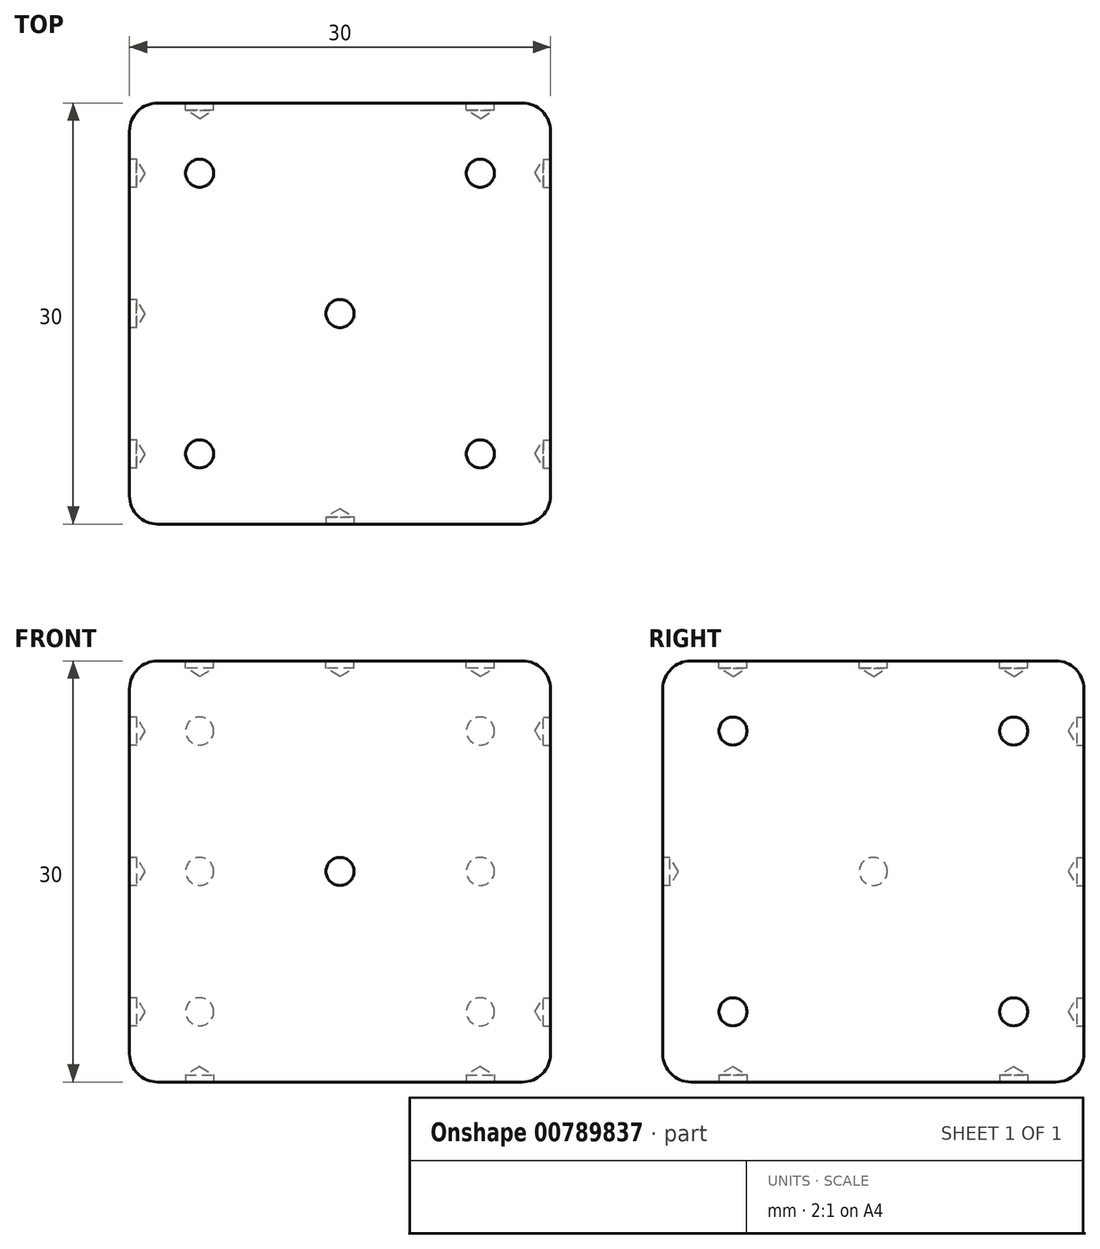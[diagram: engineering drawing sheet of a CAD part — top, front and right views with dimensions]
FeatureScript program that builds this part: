
annotation { "Feature Type Name" : "Feature", "Feature Type Description" : "" }
export const myFeature = defineFeature(function(context is Context, id is Id, definition is map)
    precondition{}
    {
        {
            var Q0;
            Q0=qCreatedBy(makeId("Front.planeOp"),FACE);
            var sketch = newSketch(context, id + "F0", { "sketchPlane" : qUnion([Q0])});
            skLineSegment(sketch, "E0.bottom", {"start": v(-16.06, 15.94) * mm, "end": v(13.94, 15.94) * mm});
            skLineSegment(sketch, "E0.top", {"start": v(-16.06, -14.06) * mm, "end": v(13.94, -14.06) * mm});
            skLineSegment(sketch, "E0.left", {"start": v(-16.06, 15.94) * mm, "end": v(-16.06, -14.06) * mm});
            skLineSegment(sketch, "E0.right", {"start": v(13.94, 15.94) * mm, "end": v(13.94, -14.06) * mm});
            skSolve(sketch);
        }
        {
            var Q0;
            Q0=makeQuery(id+"F0.imprint","IMPRINT",FACE,{"disambiguationData":[TD([[makeQuery(id+"F0.imprint","IMPRINT",EDGE,{"derivedFrom":sQuery(id+"F0.wireOp",EDGE,"E0.bottom")}),-1.0]])]});
            extrude(context, id + "F1", {"entities" : qUnion([Q0]), "endBound" : BoundingType.SYMMETRIC, "depth" : 30 * mm, "offsetDistance" : 25.4 * mm});
        }
        {
            var Q0;
            Q0=makeQuery(id+"F1.opExtrude","CAP_EDGE",EDGE,{"disambiguationData":[OSD([sQuery(id+"F0.wireOp",EDGE,"E0.bottom")])],"isStart":false});
            fillet(context, id + "F2", {"entities" : qUnion([Q0]), "radius" : 2 * mm, "tangentPropagation" : true, "allowEdgeOverflow" : false});
        }
        {
            var Q0;
            Q0=makeQuery(id+"F1.opExtrude","SWEPT_EDGE",EDGE,{"disambiguationData":[OSD([sQuery(id+"F0.wireOp",EDGE,"E0.bottom"),sQuery(id+"F0.wireOp",EDGE,"E0.right")])]});
            var Q1;
            Q1=makeQuery(id+"F1.opExtrude","CAP_EDGE",EDGE,{"disambiguationData":[OSD([sQuery(id+"F0.wireOp",EDGE,"E0.bottom")])],"isStart":true});
            var Q2;
            Q2=makeQuery(id+"F1.opExtrude","SWEPT_EDGE",EDGE,{"disambiguationData":[OSD([sQuery(id+"F0.wireOp",EDGE,"E0.bottom"),sQuery(id+"F0.wireOp",EDGE,"E0.left")])]});
            var Q3;
            Q3=makeQuery(id+"F1.opExtrude","CAP_EDGE",EDGE,{"disambiguationData":[OSD([sQuery(id+"F0.wireOp",EDGE,"E0.left")])],"isStart":true});
            var Q4;
            Q4=makeQuery(id+"F1.opExtrude","CAP_EDGE",EDGE,{"disambiguationData":[OSD([sQuery(id+"F0.wireOp",EDGE,"E0.right")])],"isStart":true});
            var Q5;
            Q5=makeQuery(id+"F1.opExtrude","CAP_EDGE",EDGE,{"disambiguationData":[OSD([sQuery(id+"F0.wireOp",EDGE,"E0.right")])],"isStart":false});
            var Q6;
            Q6=makeQuery(id+"F1.opExtrude","SWEPT_EDGE",EDGE,{"disambiguationData":[OSD([sQuery(id+"F0.wireOp",EDGE,"E0.top"),sQuery(id+"F0.wireOp",EDGE,"E0.left")])]});
            var Q7;
            Q7=makeQuery(id+"F1.opExtrude","CAP_EDGE",EDGE,{"disambiguationData":[OSD([sQuery(id+"F0.wireOp",EDGE,"E0.top")])],"isStart":true});
            var Q8;
            Q8=makeQuery(id+"F1.opExtrude","SWEPT_EDGE",EDGE,{"disambiguationData":[OSD([sQuery(id+"F0.wireOp",EDGE,"E0.top"),sQuery(id+"F0.wireOp",EDGE,"E0.right")])]});
            var Q9;
            Q9=makeQuery(id+"F1.opExtrude","CAP_EDGE",EDGE,{"disambiguationData":[OSD([sQuery(id+"F0.wireOp",EDGE,"E0.top")])],"isStart":false});
            var Q10;
            Q10=makeQuery(id+"F1.opExtrude","CAP_EDGE",EDGE,{"disambiguationData":[OSD([sQuery(id+"F0.wireOp",EDGE,"E0.left")])],"isStart":false});
            fillet(context, id + "F3", {"entities" : qUnion([Q0, Q1, Q2, Q3, Q4, Q5, Q6, Q7, Q8, Q9, Q10]), "radius" : 2 * mm, "tangentPropagation" : true, "allowEdgeOverflow" : false});
        }
        {
            var Q0;
            Q0=makeQuery(id+"F1.opExtrude","CAP_FACE",FACE,{"disambiguationData":[OSD([sQuery(id+"F0.wireOp",EDGE,"E0.bottom"),sQuery(id+"F0.wireOp",EDGE,"E0.top"),sQuery(id+"F0.wireOp",EDGE,"E0.left"),sQuery(id+"F0.wireOp",EDGE,"E0.right")])],"isStart":false});
            var sketch = newSketch(context, id + "F4", { "sketchPlane" : qUnion([Q0])});
            skCircle(sketch, "E1", {"center": v(-1.06, 0.94) * mm, "radius": 1 * mm});
            skSolve(sketch);
        }
        {
            var Q0;
            Q0=makeQuery(id+"F1.opExtrude","SWEPT_FACE",FACE,{"disambiguationData":[OSD([sQuery(id+"F0.wireOp",EDGE,"E0.bottom")])]});
            var sketch = newSketch(context, id + "F5", { "sketchPlane" : qUnion([Q0])});
            skCircle(sketch, "E2", {"center": v(-11.06, 10) * mm, "radius": 1 * mm});
            skCircle(sketch, "E3", {"center": v(8.94, 10) * mm, "radius": 1 * mm});
            skCircle(sketch, "E4", {"center": v(-11.06, -10) * mm, "radius": 1 * mm});
            skCircle(sketch, "E5", {"center": v(8.94, -10) * mm, "radius": 1 * mm});
            skCircle(sketch, "E6", {"center": v(-1.06, 0) * mm, "radius": 1 * mm});
            skSolve(sketch);
        }
        {
            var Q0;
            Q0=makeQuery(id+"F1.opExtrude","CAP_FACE",FACE,{"disambiguationData":[OSD([sQuery(id+"F0.wireOp",EDGE,"E0.bottom"),sQuery(id+"F0.wireOp",EDGE,"E0.top"),sQuery(id+"F0.wireOp",EDGE,"E0.left"),sQuery(id+"F0.wireOp",EDGE,"E0.right")])],"isStart":true});
            var sketch = newSketch(context, id + "F6", { "sketchPlane" : qUnion([Q0])});
            skCircle(sketch, "E7", {"center": v(11.06, -9.06) * mm, "radius": 1 * mm});
            skCircle(sketch, "E8", {"center": v(-8.94, -9.06) * mm, "radius": 1 * mm});
            skCircle(sketch, "E9", {"center": v(-8.94, 10.94) * mm, "radius": 1 * mm});
            skCircle(sketch, "E10", {"center": v(11.06, 10.94) * mm, "radius": 1 * mm});
            skCircle(sketch, "E11", {"center": v(11.06, 0.94) * mm, "radius": 1 * mm});
            skCircle(sketch, "E12", {"center": v(-8.94, 0.94) * mm, "radius": 1 * mm});
            skSolve(sketch);
        }
        {
            var Q0;
            Q0=makeQuery(id+"F1.opExtrude","SWEPT_FACE",FACE,{"disambiguationData":[OSD([sQuery(id+"F0.wireOp",EDGE,"E0.top")])]});
            var sketch = newSketch(context, id + "F7", { "sketchPlane" : qUnion([Q0])});
            skCircle(sketch, "E13", {"center": v(8.94, 10) * mm, "radius": 1 * mm});
            skCircle(sketch, "E14", {"center": v(-11.06, -10) * mm, "radius": 1 * mm});
            skSolve(sketch);
        }
        {
            var Q0;
            Q0=makeQuery(id+"F1.opExtrude","SWEPT_FACE",FACE,{"disambiguationData":[OSD([sQuery(id+"F0.wireOp",EDGE,"E0.right")])]});
            var sketch = newSketch(context, id + "F8", { "sketchPlane" : qUnion([Q0])});
            skCircle(sketch, "E15", {"center": v(10, 10.94) * mm, "radius": 1 * mm});
            skCircle(sketch, "E16", {"center": v(-10, 10.94) * mm, "radius": 1 * mm});
            skCircle(sketch, "E17", {"center": v(-10, -9.06) * mm, "radius": 1 * mm});
            skCircle(sketch, "E18", {"center": v(10, -9.06) * mm, "radius": 1 * mm});
            skSolve(sketch);
        }
        {
            var Q0;
            Q0=makeQuery(id+"F1.opExtrude","SWEPT_FACE",FACE,{"disambiguationData":[OSD([sQuery(id+"F0.wireOp",EDGE,"E0.left")])]});
            var sketch = newSketch(context, id + "F9", { "sketchPlane" : qUnion([Q0])});
            skCircle(sketch, "E19", {"center": v(-10, 10.94) * mm, "radius": 1 * mm});
            skCircle(sketch, "E20", {"center": v(0, 0.94) * mm, "radius": 1 * mm});
            skCircle(sketch, "E21", {"center": v(10, -9.06) * mm, "radius": 1 * mm});
            skSolve(sketch);
        }
        {
            var Q0;
            Q0=sQuery(id+"F4.wireOp",VERTEX,"E1.center");
            var Q1;
            Q1=makeQuery(id+"F1.opExtrude","SWEPT_BODY",BODY,{"disambiguationData":[OSD([sQuery(id+"F0.wireOp",EDGE,"E0.bottom"),sQuery(id+"F0.wireOp",EDGE,"E0.top"),sQuery(id+"F0.wireOp",EDGE,"E0.left"),sQuery(id+"F0.wireOp",EDGE,"E0.right")])]});
            hole(context, id + "F10", {"style" : HoleStyle.SIMPLE, "endStyle" : HoleEndStyle.BLIND, "holeDiameter" : 2 * mm, "majorDiameter" : 6.35 * mm, "holeDepth" : 0.5 * mm, "isTappedThrough" : true, "tappedDepth" : 12.7 * mm, "tapClearance" : 3, "locations" : qUnion([Q0]), "scope" : qUnion([Q1])});
        }
        {
            var Q0;
            Q0=sQuery(id+"F5.wireOp",VERTEX,"E2.center");
            var Q1;
            Q1=sQuery(id+"F5.wireOp",VERTEX,"E6.center");
            var Q2;
            Q2=sQuery(id+"F5.wireOp",VERTEX,"E3.center");
            var Q3;
            Q3=sQuery(id+"F5.wireOp",VERTEX,"E5.center");
            var Q4;
            Q4=sQuery(id+"F5.wireOp",VERTEX,"E4.center");
            var Q5;
            Q5=makeQuery(id+"F1.opExtrude","SWEPT_BODY",BODY,{"disambiguationData":[OSD([sQuery(id+"F0.wireOp",EDGE,"E0.bottom"),sQuery(id+"F0.wireOp",EDGE,"E0.top"),sQuery(id+"F0.wireOp",EDGE,"E0.left"),sQuery(id+"F0.wireOp",EDGE,"E0.right")])]});
            hole(context, id + "F11", {"style" : HoleStyle.SIMPLE, "endStyle" : HoleEndStyle.BLIND, "holeDiameter" : 2 * mm, "majorDiameter" : 6.35 * mm, "holeDepth" : 0.5 * mm, "isTappedThrough" : true, "tappedDepth" : 12.7 * mm, "tapClearance" : 3, "locations" : qUnion([Q0, Q1, Q2, Q3, Q4]), "scope" : qUnion([Q5])});
        }
        {
            var Q0;
            Q0=sQuery(id+"F6.wireOp",VERTEX,"E9.center");
            var Q1;
            Q1=sQuery(id+"F6.wireOp",VERTEX,"E12.center");
            var Q2;
            Q2=sQuery(id+"F6.wireOp",VERTEX,"E8.center");
            var Q3;
            Q3=sQuery(id+"F6.wireOp",VERTEX,"E7.center");
            var Q4;
            Q4=sQuery(id+"F6.wireOp",VERTEX,"E11.center");
            var Q5;
            Q5=sQuery(id+"F6.wireOp",VERTEX,"E10.center");
            var Q6;
            Q6=makeQuery(id+"F1.opExtrude","SWEPT_BODY",BODY,{"disambiguationData":[OSD([sQuery(id+"F0.wireOp",EDGE,"E0.bottom"),sQuery(id+"F0.wireOp",EDGE,"E0.top"),sQuery(id+"F0.wireOp",EDGE,"E0.left"),sQuery(id+"F0.wireOp",EDGE,"E0.right")])]});
            hole(context, id + "F12", {"style" : HoleStyle.SIMPLE, "endStyle" : HoleEndStyle.BLIND, "holeDiameter" : 2 * mm, "majorDiameter" : 6.35 * mm, "holeDepth" : 0.5 * mm, "isTappedThrough" : true, "tappedDepth" : 12.7 * mm, "tapClearance" : 3, "locations" : qUnion([Q0, Q1, Q2, Q3, Q4, Q5]), "scope" : qUnion([Q6])});
        }
        {
            var Q0;
            Q0=sQuery(id+"F7.wireOp",VERTEX,"E13.center");
            var Q1;
            Q1=sQuery(id+"F7.wireOp",VERTEX,"E14.center");
            var Q2;
            Q2=makeQuery(id+"F1.opExtrude","SWEPT_BODY",BODY,{"disambiguationData":[OSD([sQuery(id+"F0.wireOp",EDGE,"E0.bottom"),sQuery(id+"F0.wireOp",EDGE,"E0.top"),sQuery(id+"F0.wireOp",EDGE,"E0.left"),sQuery(id+"F0.wireOp",EDGE,"E0.right")])]});
            hole(context, id + "F13", {"style" : HoleStyle.SIMPLE, "endStyle" : HoleEndStyle.BLIND, "holeDiameter" : 2 * mm, "majorDiameter" : 6.35 * mm, "holeDepth" : 0.5 * mm, "isTappedThrough" : true, "tappedDepth" : 12.7 * mm, "tapClearance" : 3, "locations" : qUnion([Q0, Q1]), "scope" : qUnion([Q2])});
        }
        {
            var Q0;
            Q0=sQuery(id+"F8.wireOp",VERTEX,"E16.center");
            var Q1;
            Q1=sQuery(id+"F8.wireOp",VERTEX,"E17.center");
            var Q2;
            Q2=sQuery(id+"F8.wireOp",VERTEX,"E18.center");
            var Q3;
            Q3=sQuery(id+"F8.wireOp",VERTEX,"E15.center");
            var Q4;
            Q4=makeQuery(id+"F1.opExtrude","SWEPT_BODY",BODY,{"disambiguationData":[OSD([sQuery(id+"F0.wireOp",EDGE,"E0.bottom"),sQuery(id+"F0.wireOp",EDGE,"E0.top"),sQuery(id+"F0.wireOp",EDGE,"E0.left"),sQuery(id+"F0.wireOp",EDGE,"E0.right")])]});
            hole(context, id + "F14", {"style" : HoleStyle.SIMPLE, "endStyle" : HoleEndStyle.BLIND, "holeDiameter" : 2 * mm, "majorDiameter" : 6.35 * mm, "holeDepth" : 0.5 * mm, "isTappedThrough" : true, "tappedDepth" : 12.7 * mm, "tapClearance" : 3, "locations" : qUnion([Q0, Q1, Q2, Q3]), "scope" : qUnion([Q4])});
        }
        {
            var Q0;
            Q0=sQuery(id+"F9.wireOp",VERTEX,"E19.center");
            var Q1;
            Q1=sQuery(id+"F9.wireOp",VERTEX,"E20.center");
            var Q2;
            Q2=sQuery(id+"F9.wireOp",VERTEX,"E21.center");
            var Q3;
            Q3=makeQuery(id+"F1.opExtrude","SWEPT_BODY",BODY,{"disambiguationData":[OSD([sQuery(id+"F0.wireOp",EDGE,"E0.bottom"),sQuery(id+"F0.wireOp",EDGE,"E0.top"),sQuery(id+"F0.wireOp",EDGE,"E0.left"),sQuery(id+"F0.wireOp",EDGE,"E0.right")])]});
            hole(context, id + "F15", {"style" : HoleStyle.SIMPLE, "endStyle" : HoleEndStyle.BLIND, "holeDiameter" : 2 * mm, "majorDiameter" : 6.35 * mm, "holeDepth" : 0.5 * mm, "isTappedThrough" : true, "tappedDepth" : 12.7 * mm, "tapClearance" : 3, "locations" : qUnion([Q0, Q1, Q2]), "scope" : qUnion([Q3])});
        }
    });
